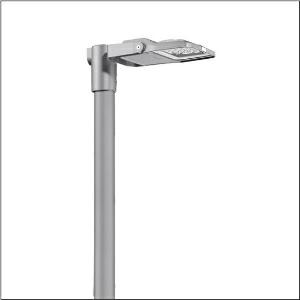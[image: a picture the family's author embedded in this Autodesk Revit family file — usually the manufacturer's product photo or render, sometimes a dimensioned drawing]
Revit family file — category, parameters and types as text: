
# Revit family: floodlight_fl_21_iq_micro___pl43_5xa7762a4a3a_9a39
name_source: partatom
category: Lighting Fixtures
units: mm (PartAtom-declared; Revit-internal decimal feet)

## family parameters
Cut with Voids When Loaded = No
Host = Face
Light Source = No
Part Type = Normal
Room Calculation Point = No
Round Connector Dimension = Use Diameter
Shared = No

## types (1)
- --- (1 x LED, 3170 lm, 23.1 W, 4000K)
    Apparent Load = 23 VA
    CIE Flux Codes = 29 80 99 100 100
    Color Rendering = 70
    Color Temperature = 4000K
    Default Elevation = 1800 mm
    Description = Floodlight FL 21 iQ micro, floodlight, primary light control with lens, of PMMA, primary optical cover: protective disc, of toughened safety glass, transparent, light distribution: PL43, light emission: direct distribution, installation type: surface-mounted, LED, High Power LED, rated luminous flux: 3.170lm, luminous efficacy: 137lm/W, light colour: 740, colour temperature: 4000K, control: Auto-Match, Temp-Guard, Night-Set, Smart-Wire, Desk-Remote (wireless, voltage-free reading and setting of iQ features in the workshop via application-optimized NFC function/RFID function), optimised constant luminous flux control (CLO 2.0), Street-Remote, with terminal, 6-pole, mains connection: 220..240V, AC, 50/60Hz, start of lifetime: 23W, end of service life: 24W, reduction: 11W, luminaire housing, of diecast aluminium, powder-coated, Siteco® metallic grey (DB 702S), corrosivity category C5 mid according to DIN EN ISO 12944, sealing non-destructively replaceable, please order mast flange separately, mast bracket, of steel, galvanised, powder-coated, Siteco® metallic grey (DB 702S), protection rating (complete): IP66, insulation class (complete): insulation class II (safety insulation), certification: CE, ENEC, VDE, protection symbol: D, impact resistance: IK07, permissible operating ambient temperature: -40..+40°C, permissible operating ambient temperature for outdoor applications: -40..+50°C, standard: DIN EN 12944, LABS conformity tested according to VDMA 24364:2018-05, packaging unit: 1 piece

Light Distribution: PL43
    Height = 65 mm
    Lamp = 1 x LED
    Lamp Light Flux = 3170 lm
    Lamp Power = 23.1 W
    Lamp count = 1
    Length = 312 mm
    Luminous efficacy = 137 lm/W
    Manufacturer = Siteco
    ModVariant = No
    Model = 5XA7762A4A3A
    Number of Poles = 1
    OnlyDefault = Yes
    Power Factor = 1
    Product Name = Floodlight FL 21 iQ micro | PL43
    Product group = floodlight | pylon annexe
    ProductGroupID = 6200
    Protection Class = Protection class II
    Protection Degree = IP 66
    RLX_Detail_Level = 1
    RLX_Emergency_Light_Flux = 0 lm
    RLX_Emergency_Type = 0
    RLX_Emergency_Type_DB = No
    RlxData = <blob elided: 101817 chars, md5=20c3ed28>
    Socket = socket
    Standby Power = 0 W
    System Light Flux = 3170 lm
    System Power = 23 W
    Type Comments = factory setting: luminous flux: 100 % | dim-lin: 254 | 455 mA
    Type Image = l_1007121.jpg
    URL = http://relux.com
    VarID = @adj_109841
    Voltage = 0 V
    Weight = 0.00 kg
    Width = 230 mm

## geometry (parser evidence)
native form markers: Blend x4, Sweep x11
no freeform markers — native parametric forms only
